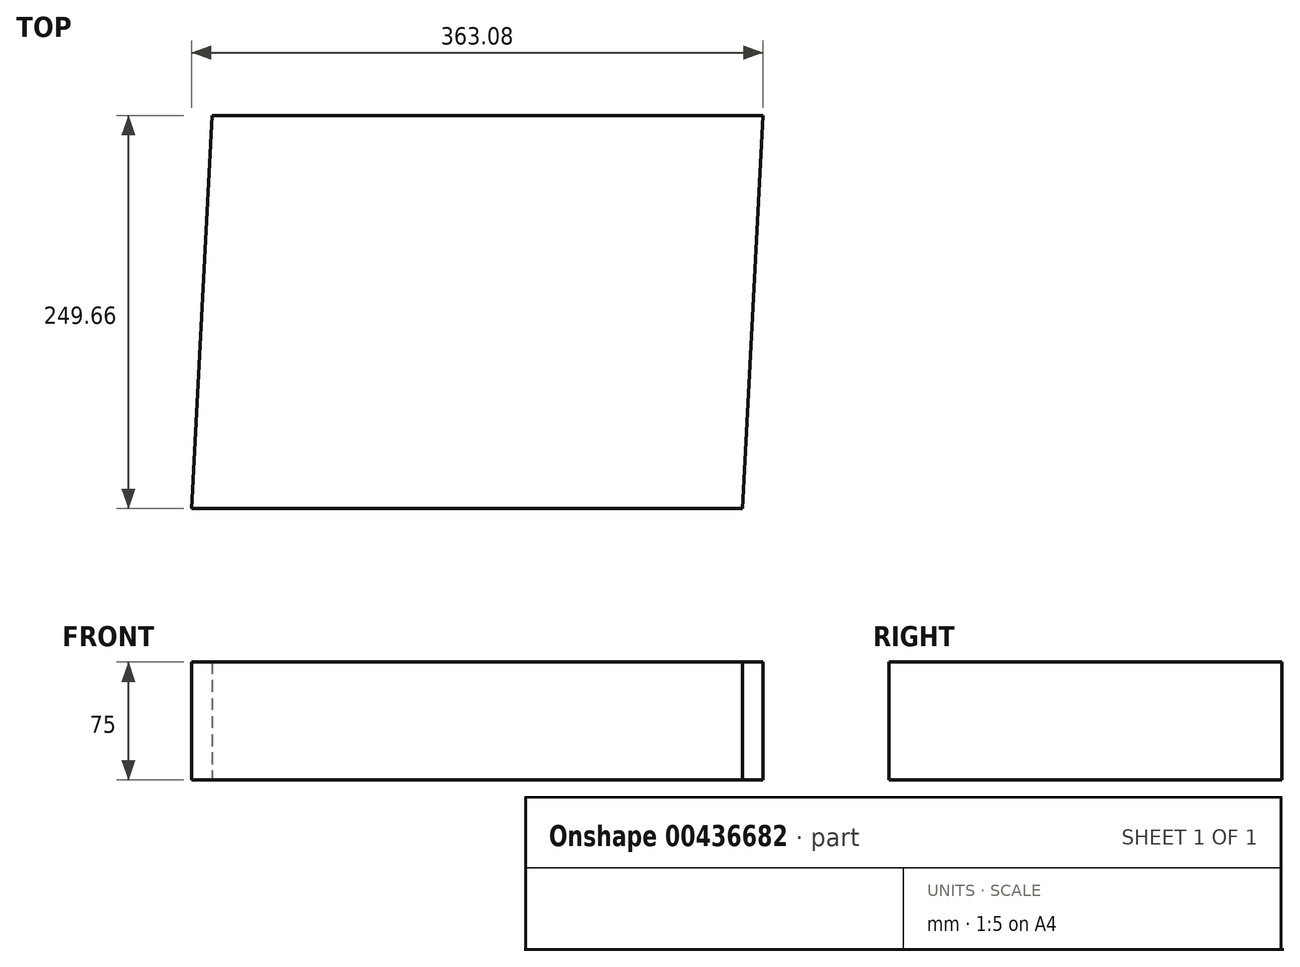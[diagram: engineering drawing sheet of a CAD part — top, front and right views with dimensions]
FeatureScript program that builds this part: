
annotation { "Feature Type Name" : "Feature", "Feature Type Description" : "" }
export const myFeature = defineFeature(function(context is Context, id is Id, definition is map)
    precondition{}
    {
        {
            var Q0;
            Q0=qCreatedBy(makeId("Top.planeOp"),FACE);
            var sketch = newSketch(context, id + "F0", { "sketchPlane" : qUnion([Q0])});
            skLineSegment(sketch, "E0.bottom", {"start": v(168.46, -124.83) * mm, "end": v(-181.54, -124.83) * mm});
            skLineSegment(sketch, "E0.top", {"start": v(181.54, 124.83) * mm, "end": v(-168.46, 124.83) * mm});
            skLineSegment(sketch, "E0.left", {"start": v(168.46, -124.83) * mm, "end": v(181.54, 124.83) * mm});
            skLineSegment(sketch, "E0.right", {"start": v(-181.54, -124.83) * mm, "end": v(-168.46, 124.83) * mm});
            skPoint(sketch, "E0.middle", {"position": v(0, 0) * mm});
            skSolve(sketch);
        }
        {
            var Q0;
            Q0=qSketchRegion(id+"F0",true);
            extrude(context, id + "F1", {"entities" : qUnion([Q0]), "depth" : 75 * mm});
        }
    });
